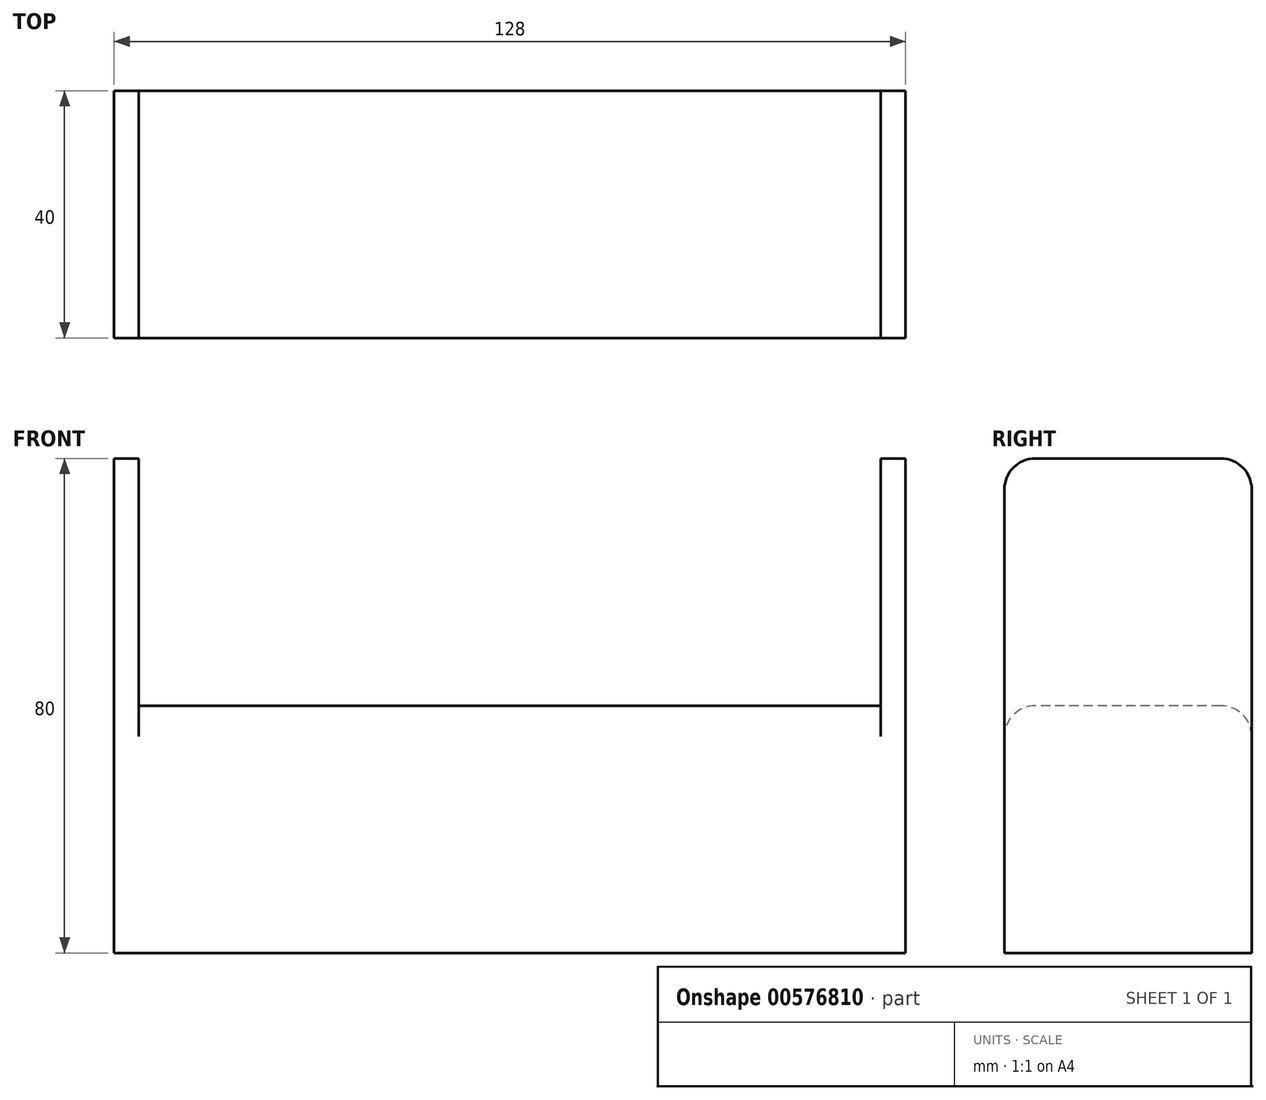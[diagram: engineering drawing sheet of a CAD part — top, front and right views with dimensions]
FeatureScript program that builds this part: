
annotation { "Feature Type Name" : "Feature", "Feature Type Description" : "" }
export const myFeature = defineFeature(function(context is Context, id is Id, definition is map)
    precondition{}
    {
        {
            assignVariable(context, id + "F0", {"name" : "H", "anyValue" : 40});
        }
        {
            var Q0;
            Q0=qCreatedBy(makeId("Top.planeOp"),FACE);
            var sketch = newSketch(context, id + "F1", { "sketchPlane" : qUnion([Q0])});
            skLineSegment(sketch, "E0.bottom", {"start": v(-120, 0) * mm, "end": v(0, 0) * mm});
            skLineSegment(sketch, "E0.top", {"start": v(-120, -40) * mm, "end": v(0, -40) * mm});
            skLineSegment(sketch, "E0.left", {"start": v(-120, 0) * mm, "end": v(-120, -40) * mm});
            skLineSegment(sketch, "E0.right", {"start": v(0, 0) * mm, "end": v(0, -40) * mm});
            skLineSegment(sketch, "E1.bottom", {"start": v(0, -40) * mm, "end": v(4, -40) * mm});
            skLineSegment(sketch, "E1.top", {"start": v(0, 0) * mm, "end": v(4, 0) * mm});
            skLineSegment(sketch, "E1.left", {"start": v(0, -40) * mm, "end": v(0, 0) * mm});
            skLineSegment(sketch, "E1.right", {"start": v(4, -40) * mm, "end": v(4, 0) * mm});
            skLineSegment(sketch, "E2.left", {"start": v(-125.55, -40) * mm, "end": v(-125.55, -40) * mm});
            skLineSegment(sketch, "E2.right", {"start": v(-120, -40) * mm, "end": v(-120, -40) * mm});
            skLineSegment(sketch, "E3.bottom", {"start": v(-120, -40) * mm, "end": v(-124, -40) * mm});
            skLineSegment(sketch, "E3.top", {"start": v(-120, 0) * mm, "end": v(-124, 0) * mm});
            skLineSegment(sketch, "E3.left", {"start": v(-120, -40) * mm, "end": v(-120, 0) * mm});
            skLineSegment(sketch, "E3.right", {"start": v(-124, -40) * mm, "end": v(-124, 0) * mm});
            skSolve(sketch);
        }
        {
            var Q0;
            Q0=makeQuery(id+"F1.imprint","IMPRINT",FACE,{"disambiguationData":[TD([[makeQuery(id+"F1.imprint","IMPRINT",EDGE,{"derivedFrom":sQuery(id+"F1.wireOp",EDGE,"E0.bottom")}),-1.0]])]});
            extrude(context, id + "F2", {"entities" : qUnion([Q0]), "depth" : getVariable(context, 'H') * mm, "offsetDistance" : 25 * mm});
        }
        {
            var Q0;
            Q0=makeQuery(id+"F1.imprint","IMPRINT",FACE,{"disambiguationData":[TD([[makeQuery(id+"F1.imprint","IMPRINT",EDGE,{"derivedFrom":sQuery(id+"F1.wireOp",EDGE,"E1.bottom")}),1.0]])]});
            var Q1;
            Q1=makeQuery(id+"F1.imprint","IMPRINT",FACE,{"disambiguationData":[TD([[makeQuery(id+"F1.imprint","IMPRINT",EDGE,{"derivedFrom":sQuery(id+"F1.wireOp",EDGE,"E3.bottom")}),-1.0]])]});
            extrude(context, id + "F3", {"entities" : qUnion([Q0, Q1]), "operationType" : NewBodyOperationType.ADD, "depth" : 80 * mm, "offsetDistance" : 25 * mm});
        }
        {
            var Q0;
            Q0=makeQuery(id+"F2.opExtrude","CAP_EDGE",EDGE,{"disambiguationData":[OSD([sQuery(id+"F1.wireOp",EDGE,"E0.top")])],"isStart":false});
            var Q1;
            Q1=makeQuery(id+"F2.opExtrude","CAP_EDGE",EDGE,{"disambiguationData":[OSD([sQuery(id+"F1.wireOp",EDGE,"E0.bottom")])],"isStart":false});
            var Q2;
            Q2=makeQuery(id+"F3.opExtrude","CAP_EDGE",EDGE,{"disambiguationData":[OSD([sQuery(id+"F1.wireOp",EDGE,"E3.bottom")])],"isStart":false});
            var Q3;
            Q3=makeQuery(id+"F3.opExtrude","CAP_EDGE",EDGE,{"disambiguationData":[OSD([sQuery(id+"F1.wireOp",EDGE,"E3.top")])],"isStart":false});
            var Q4;
            Q4=makeQuery(id+"F3.opExtrude","CAP_EDGE",EDGE,{"disambiguationData":[OSD([sQuery(id+"F1.wireOp",EDGE,"E1.bottom")])],"isStart":false});
            var Q5;
            Q5=makeQuery(id+"F3.opExtrude","CAP_EDGE",EDGE,{"disambiguationData":[OSD([sQuery(id+"F1.wireOp",EDGE,"E1.top")])],"isStart":false});
            fillet(context, id + "F4", {"entities" : qUnion([Q0, Q1, Q2, Q3, Q4, Q5]), "radius" : 5 * mm, "tangentPropagation" : true, "allowEdgeOverflow" : false});
        }
    });
